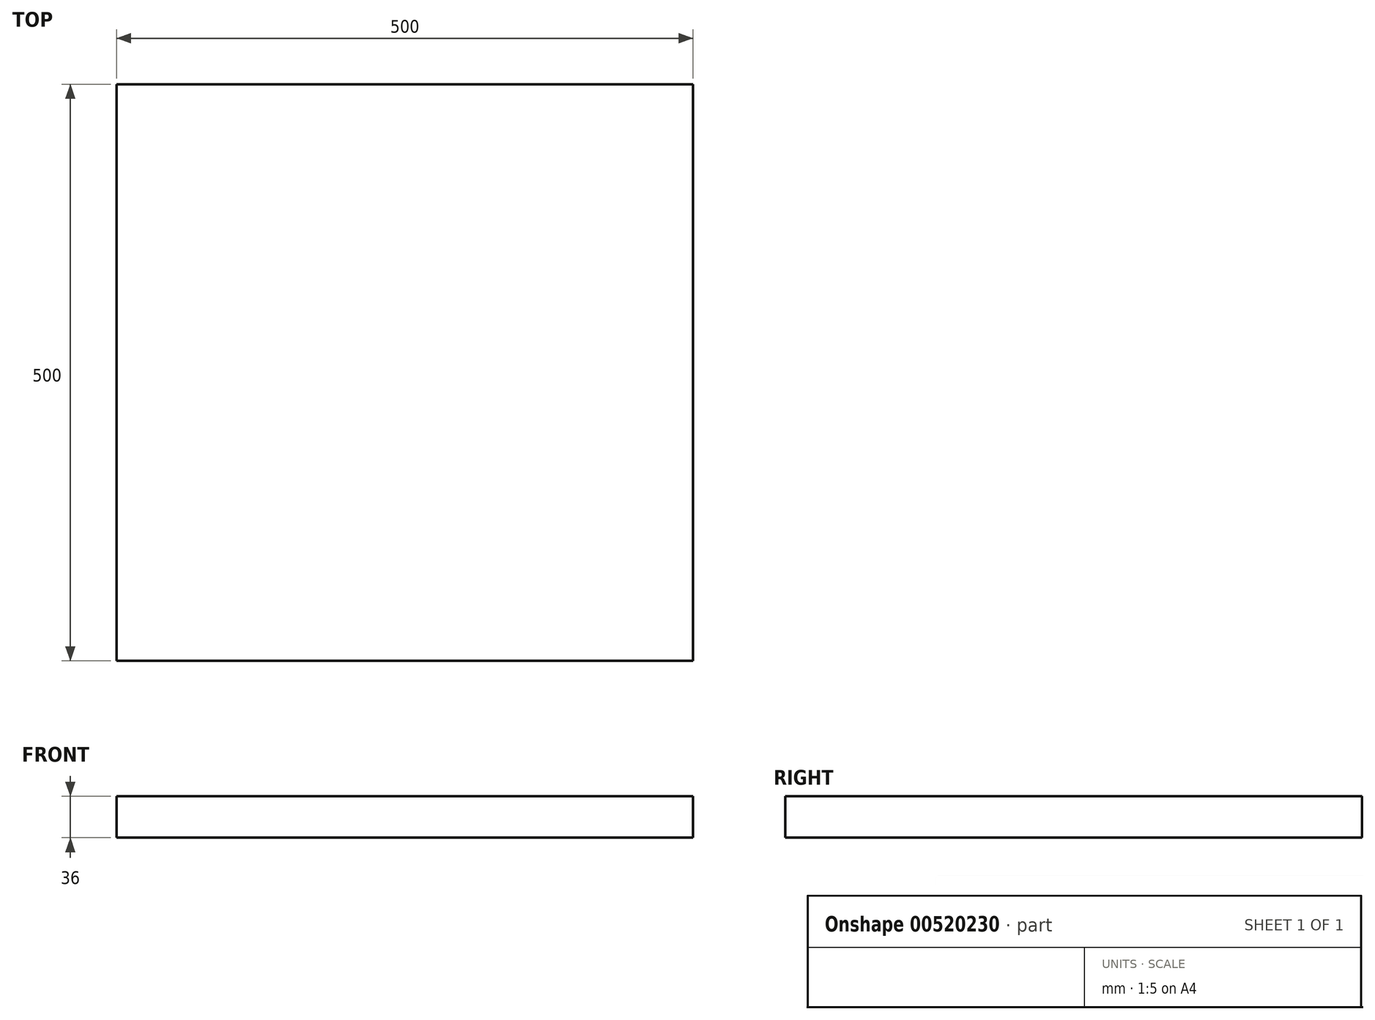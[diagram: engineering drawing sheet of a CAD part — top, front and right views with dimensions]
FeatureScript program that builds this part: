
annotation { "Feature Type Name" : "Feature", "Feature Type Description" : "" }
export const myFeature = defineFeature(function(context is Context, id is Id, definition is map)
    precondition{}
    {
        {
            var Q0;
            Q0=qCreatedBy(makeId("Top.planeOp"),FACE);
            var sketch = newSketch(context, id + "F0", { "sketchPlane" : qUnion([Q0])});
            skLineSegment(sketch, "E0.bottom", {"start": v(-215.37, 283.35) * mm, "end": v(284.63, 283.35) * mm});
            skLineSegment(sketch, "E0.top", {"start": v(-215.37, -216.65) * mm, "end": v(284.63, -216.65) * mm});
            skLineSegment(sketch, "E0.left", {"start": v(-215.37, 283.35) * mm, "end": v(-215.37, -216.65) * mm});
            skLineSegment(sketch, "E0.right", {"start": v(284.63, 283.35) * mm, "end": v(284.63, -216.65) * mm});
            skSolve(sketch);
        }
        {
            var Q0;
            Q0 = qSketchRegion(id + "F0", true);
            extrude(context, id + "F1", {"entities" : qUnion([Q0]), "oppositeDirection" : true, "depth" : 36 * mm, "offsetDistance" : 25 * mm});
        }
    });
